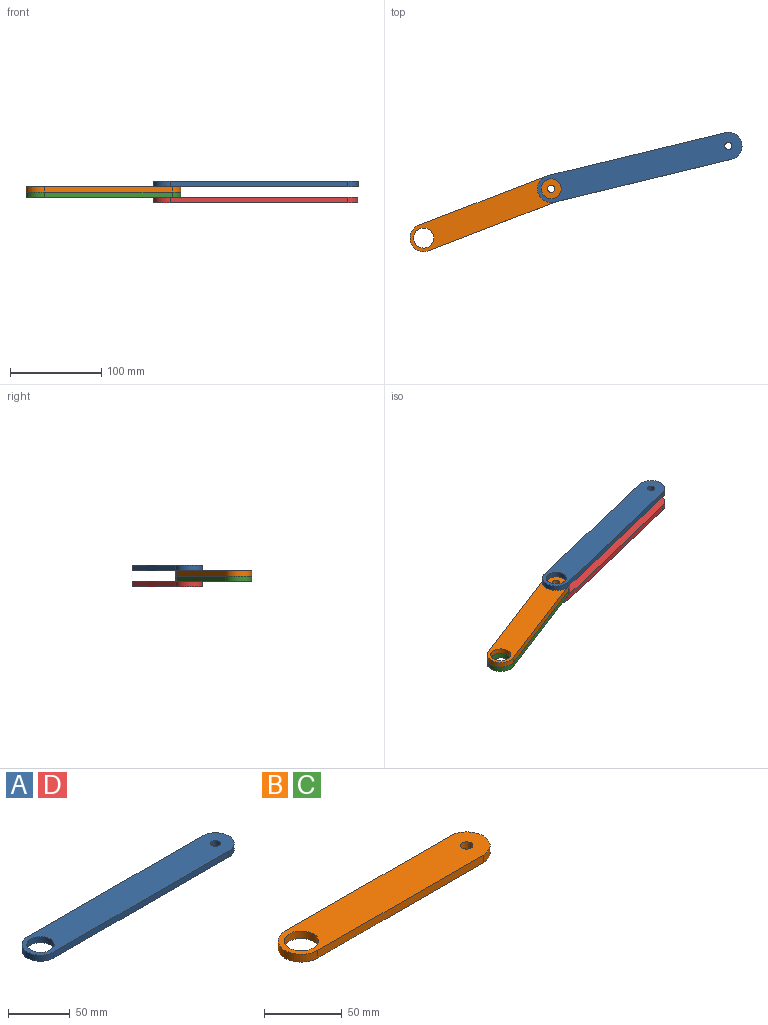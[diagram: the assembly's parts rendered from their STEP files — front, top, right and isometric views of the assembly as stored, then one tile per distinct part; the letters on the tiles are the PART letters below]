
ASSEMBLY  parts=4 mates=4
PART A: 8 faces, bbox 230x30x6 mm
  f0: plane 200x6mm, normal (0,1,0), area 1200mm2, adj f1,f5,f6,f7
  f1: cylinder r=15mm len=30mm, axis (0,0,-1), area 282.7mm2, adj f0,f2,f6,f7
  f2: plane 200x6mm, normal (0,-1,0), area 1200mm2, adj f1,f5,f6,f7
  f3: cylinder r=11mm len=22mm, axis (0,0,-1), area 414.7mm2, adj f6,f7
  f4: cylinder r=4mm len=8mm, axis (0,0,-1), area 150.8mm2, adj f6,f7
  f5: cylinder r=15mm len=30mm, axis (0,0,-1), area 282.7mm2, adj f0,f2,f6,f7
  f6: plane 230x30mm, normal (0,0,1), area 6276.5mm2, adj f0,f1,f2,f3,f4,f5
  f7: plane 230x30mm, normal (0,0,-1), area 6276.5mm2, adj f0,f1,f2,f3,f4,f5
PART B: 8 faces, bbox 180x30x6 mm
  f0: plane 150x6mm, normal (0,1,0), area 900mm2, adj f1,f5,f6,f7
  f1: cylinder r=15mm len=30mm, axis (0,0,-1), area 282.7mm2, adj f0,f2,f6,f7
  f2: plane 150x6mm, normal (0,-1,0), area 900mm2, adj f1,f5,f6,f7
  f3: cylinder r=11mm len=22mm, axis (0,0,-1), area 414.7mm2, adj f6,f7
  f4: cylinder r=4mm len=8mm, axis (0,0,-1), area 150.8mm2, adj f6,f7
  f5: cylinder r=15mm len=30mm, axis (0,0,-1), area 282.7mm2, adj f0,f2,f6,f7
  f6: plane 180x30mm, normal (0,0,1), area 4776.5mm2, adj f0,f1,f2,f3,f4,f5
  f7: plane 180x30mm, normal (0,0,-1), area 4776.5mm2, adj f0,f1,f2,f3,f4,f5
PART C: same geometry as B
PART D: same geometry as A
PLACE A rot(axis=(0,0,1),13.6deg) t=(177.61,86.98,22.26)mm
PLACE B rot(axis=(0,0,1),21.1deg) t=(10.44,36.46,16.26)mm
PLACE C rot(axis=(0,0,1),21.1deg) t=(10.44,36.46,10.26)mm fixed
PLACE D rot(axis=(0,0,1),13.6deg) t=(177.61,86.98,4.26)mm
MATE fastened B.f7 <-> C.f6  axis (0,0,-1) through (15.27,38.32,16.26)mm
MATE slider A.f7 <-> D.f6  axis (0,0,-1) through (182.72,88.22,22.26)mm
MATE revolute D.f3 <-> C.f4  axis (0,0,-1) through (80.42,63.43,10.26)mm
MATE revolute B.f5 <-> A.f3  axis (0,0,1) through (80.42,63.43,22.26)mm
